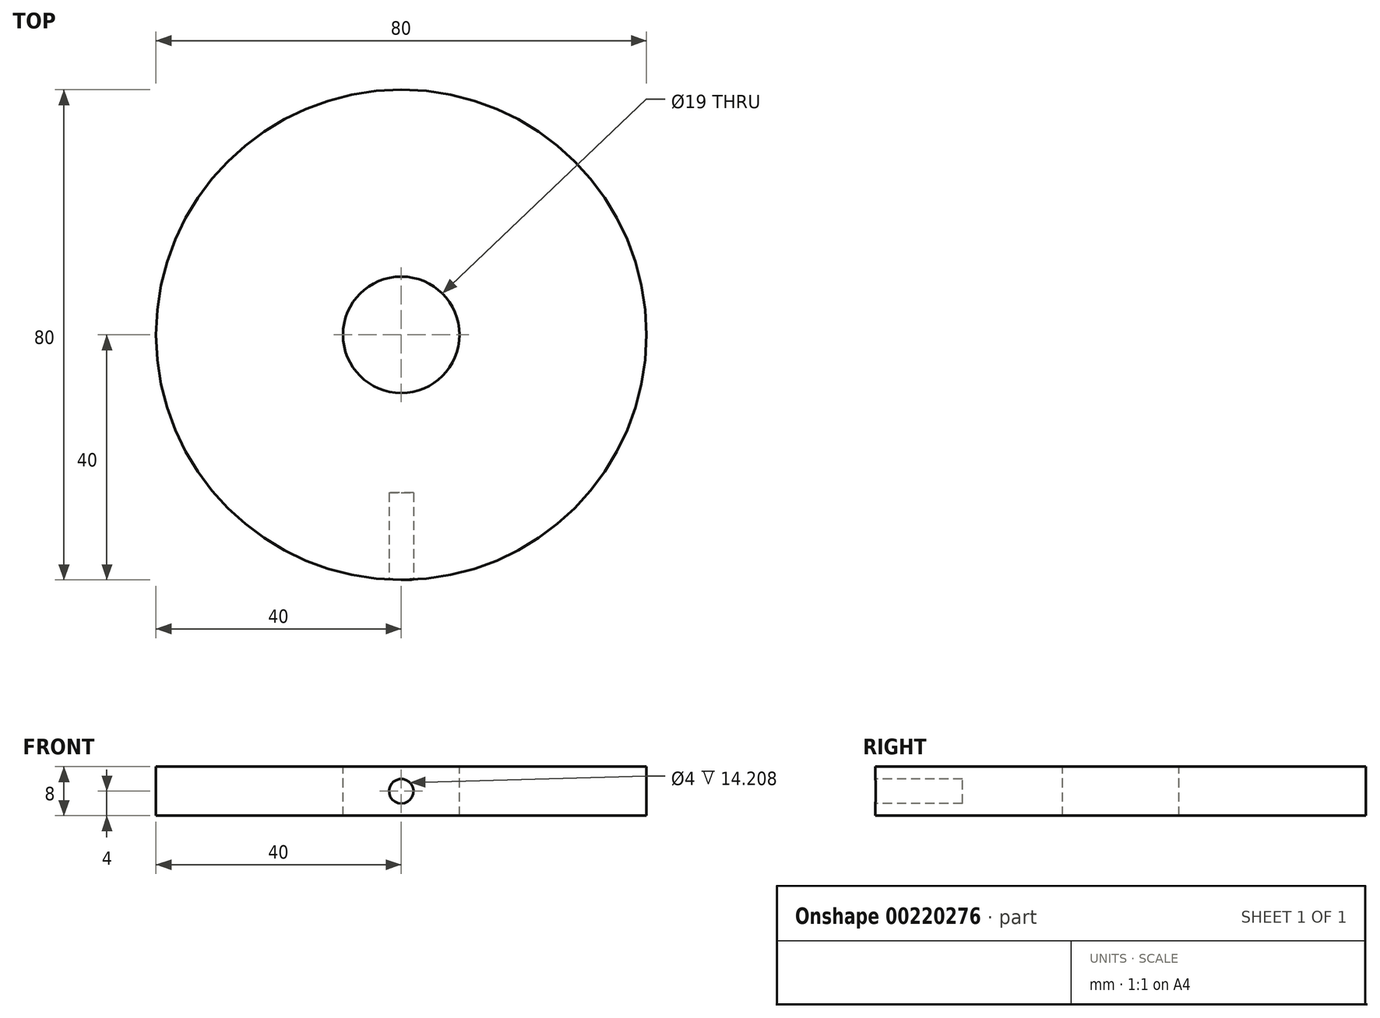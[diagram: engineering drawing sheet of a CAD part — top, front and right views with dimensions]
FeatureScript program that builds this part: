
annotation { "Feature Type Name" : "Feature", "Feature Type Description" : "" }
export const myFeature = defineFeature(function(context is Context, id is Id, definition is map)
    precondition{}
    {
        {
            var Q0;
            Q0=qCreatedBy(makeId("Top.planeOp"),FACE);
            var sketch = newSketch(context, id + "F0", { "sketchPlane" : qUnion([Q0])});
            skCircle(sketch, "E0", {"center": v(0, 0) * mm, "radius": 40 * mm});
            skSolve(sketch);
        }
        {
            var Q0;
            Q0=qSketchRegion(id+"F0",true);
            extrude(context, id + "F1", {"entities" : qUnion([Q0]), "depth" : 8 * mm});
        }
        {
            var Q0;
            Q0=makeQuery(id+"F1.opExtrude","CAP_FACE",FACE,{"disambiguationData":[OSD([sQuery(id+"F0.wireOp",EDGE,"E0")])],"isStart":false});
            var sketch = newSketch(context, id + "F2", { "sketchPlane" : qUnion([Q0])});
            skCircle(sketch, "E1", {"center": v(0, 0) * mm, "radius": 9.5 * mm});
            skSolve(sketch);
        }
        {
            var Q0;
            Q0=makeQuery(id+"F2.imprint","IMPRINT",FACE,{"disambiguationData":[TD([[makeQuery(id+"F2.imprint","IMPRINT",EDGE,{"derivedFrom":sQuery(id+"F2.wireOp",EDGE,"E1")}),1.0]])]});
            var Q1;
            Q1=sQuery(id+"F2.wireOp",EDGE,"E1");
            extrude(context, id + "F3", {"entities" : qUnion([Q0]), "operationType" : NewBodyOperationType.REMOVE, "surfaceEntities" : qUnion([Q1]), "endBound" : BoundingType.THROUGH_ALL, "oppositeDirection" : true, "depth" : 25 * mm});
        }
        {
            var Q0;
            Q0=makeQuery(id+"F1.opExtrude","CAP_FACE",FACE,{"disambiguationData":[OSD([sQuery(id+"F0.wireOp",EDGE,"E0")])],"isStart":false});
            var sketch = newSketch(context, id + "F4", { "sketchPlane" : qUnion([Q0])});
            skPoint(sketch, "E2", {"position": v(14.5, 0) * mm});
            skPoint(sketch, "E3", {"position": v(0, -20.49) * mm});
            skPoint(sketch, "E4.MirrorP", {"position": v(-14.5, 0) * mm});
            skSolve(sketch);
        }
        {
            var Q0;
            Q0=qCreatedBy(makeId("Front.planeOp"),FACE);
            cPlane(context, id + "F5", {"entities" : qUnion([Q0]), "cplaneType" : CPlaneType.OFFSET, "offset" : 40.8 * mm, "width" : 150 * mm, "height" : 150 * mm});
        }
        {
            var Q0;
            Q0=qCreatedBy(id+"F5.planeOp",FACE);
            var sketch = newSketch(context, id + "F6", { "sketchPlane" : qUnion([Q0])});
            skCircle(sketch, "E5", {"center": v(0, 4) * mm, "radius": 2 * mm});
            skSolve(sketch);
        }
        {
            var Q0;
            Q0=qSketchRegion(id+"F6",true);
            extrude(context, id + "F7", {"entities" : qUnion([Q0]), "operationType" : NewBodyOperationType.REMOVE, "oppositeDirection" : true, "depth" : 15 * mm});
        }
    });
